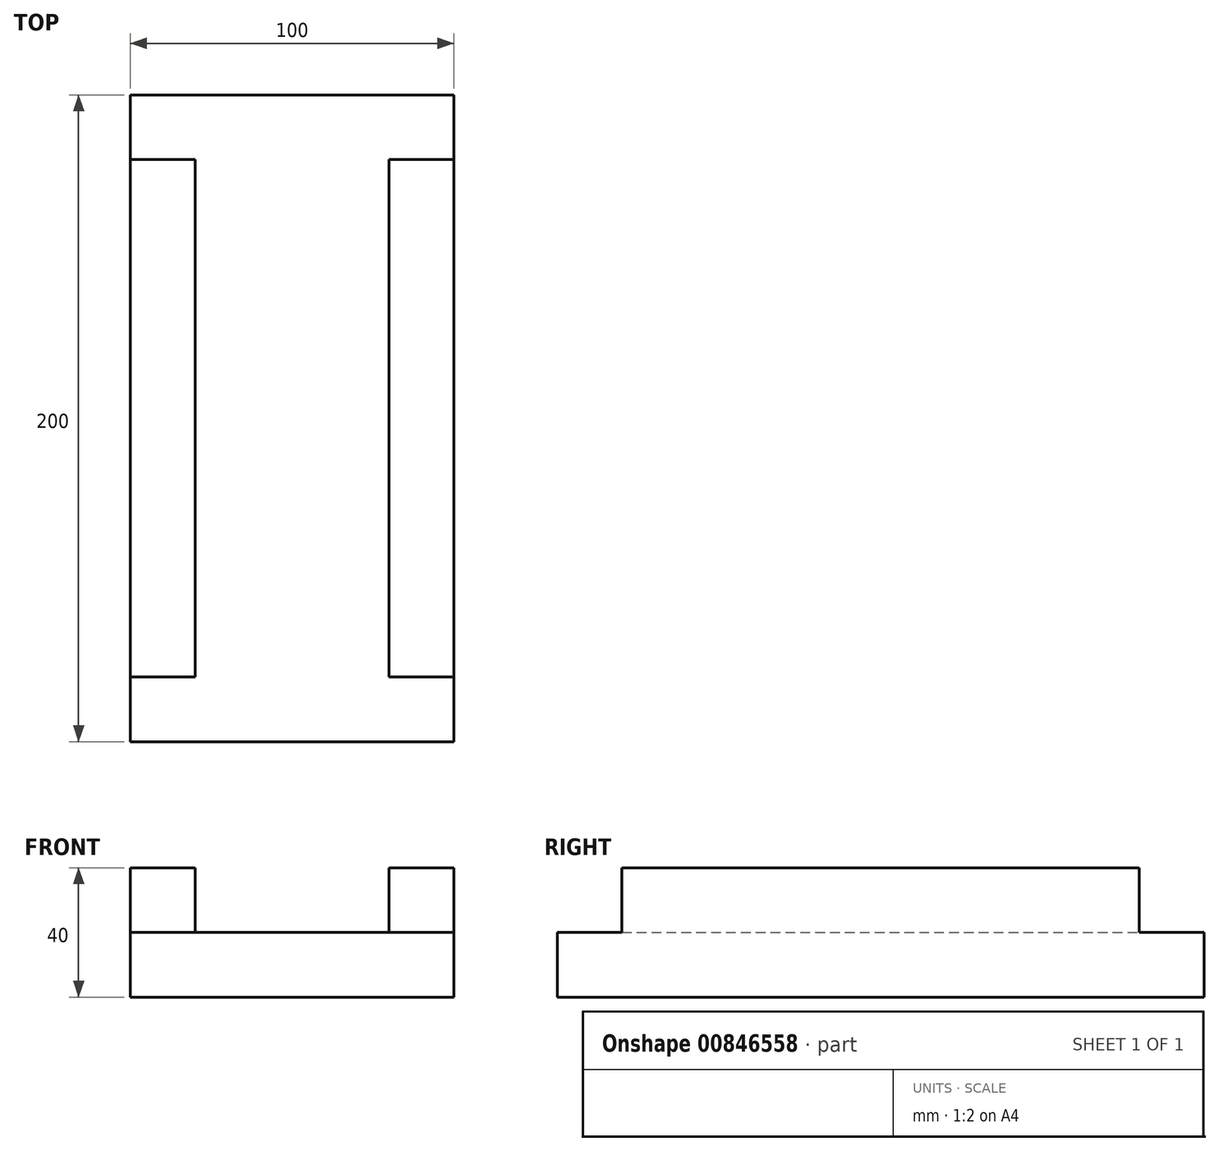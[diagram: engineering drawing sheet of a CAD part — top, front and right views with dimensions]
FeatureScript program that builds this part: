
annotation { "Feature Type Name" : "Feature", "Feature Type Description" : "" }
export const myFeature = defineFeature(function(context is Context, id is Id, definition is map)
    precondition{}
    {
        {
            var Q0;
            Q0=qCreatedBy(makeId("Top.planeOp"),FACE);
            var sketch = newSketch(context, id + "F0", { "sketchPlane" : qUnion([Q0])});
            skLineSegment(sketch, "E0", {"start": v(-72.94, 124.95) * mm, "end": v(-72.94, -75.05) * mm});
            skLineSegment(sketch, "E1", {"start": v(-72.94, -75.05) * mm, "end": v(27.06, -75.05) * mm});
            skLineSegment(sketch, "E2", {"start": v(27.06, -75.05) * mm, "end": v(27.06, 124.95) * mm});
            skLineSegment(sketch, "E3", {"start": v(27.06, 124.95) * mm, "end": v(-72.94, 124.95) * mm});
            skSolve(sketch);
        }
        {
            var Q0;
            Q0 = qSketchRegion(id + "F0", true);
            extrude(context, id + "F1", {"entities" : qUnion([Q0]), "depth" : 20 * mm, "offsetDistance" : 25 * mm});
        }
        {
            var Q0;
            Q0=makeQuery(id+"F1.opExtrude","CAP_FACE",FACE,{"disambiguationData":[OSD([sQuery(id+"F0.wireOp",EDGE,"E0"),sQuery(id+"F0.wireOp",EDGE,"E1"),sQuery(id+"F0.wireOp",EDGE,"E2"),sQuery(id+"F0.wireOp",EDGE,"E3")])],"isStart":false});
            var sketch = newSketch(context, id + "F2", { "sketchPlane" : qUnion([Q0])});
            skLineSegment(sketch, "E4", {"start": v(-52.94, 104.95) * mm, "end": v(-52.94, -55.05) * mm});
            skLineSegment(sketch, "E5", {"start": v(-52.94, -55.05) * mm, "end": v(7.06, -55.05) * mm});
            skLineSegment(sketch, "E6", {"start": v(7.06, -55.05) * mm, "end": v(7.06, 104.95) * mm});
            skLineSegment(sketch, "E7", {"start": v(7.06, 104.95) * mm, "end": v(-52.94, 104.95) * mm});
            skLineSegment(sketch, "E8", {"start": v(-52.94, 104.95) * mm, "end": v(-72.94, 104.95) * mm});
            skPoint(sketch, "E8.endSnap0", {"position": v(-72.94, 24.95) * mm});
            skLineSegment(sketch, "E9", {"start": v(-72.94, 104.95) * mm, "end": v(-72.94, -55.05) * mm});
            skLineSegment(sketch, "E10", {"start": v(-72.94, -55.05) * mm, "end": v(-52.94, -55.05) * mm});
            skLineSegment(sketch, "E11", {"start": v(7.06, 104.95) * mm, "end": v(27.06, 104.95) * mm});
            skLineSegment(sketch, "E12", {"start": v(27.06, 104.95) * mm, "end": v(27.06, -55.05) * mm});
            skLineSegment(sketch, "E13", {"start": v(27.06, -55.05) * mm, "end": v(7.06, -55.05) * mm});
            skSolve(sketch);
        }
        {
            var Q0;
            Q0=makeQuery(id+"F2.imprint","IMPRINT",FACE,{"disambiguationData":[TD([[makeQuery(id+"F2.imprint","IMPRINT",EDGE,{"derivedFrom":sQuery(id+"F2.wireOp",EDGE,"E4")}),-1.0]])]});
            var Q1;
            Q1=makeQuery(id+"F2.imprint","IMPRINT",FACE,{"disambiguationData":[TD([[makeQuery(id+"F2.imprint","IMPRINT",EDGE,{"derivedFrom":sQuery(id+"F2.wireOp",EDGE,"E6")}),-1.0]])]});
            extrude(context, id + "F3", {"entities" : qUnion([Q0, Q1]), "operationType" : NewBodyOperationType.ADD, "depth" : 20 * mm, "offsetDistance" : 25 * mm});
        }
    });
